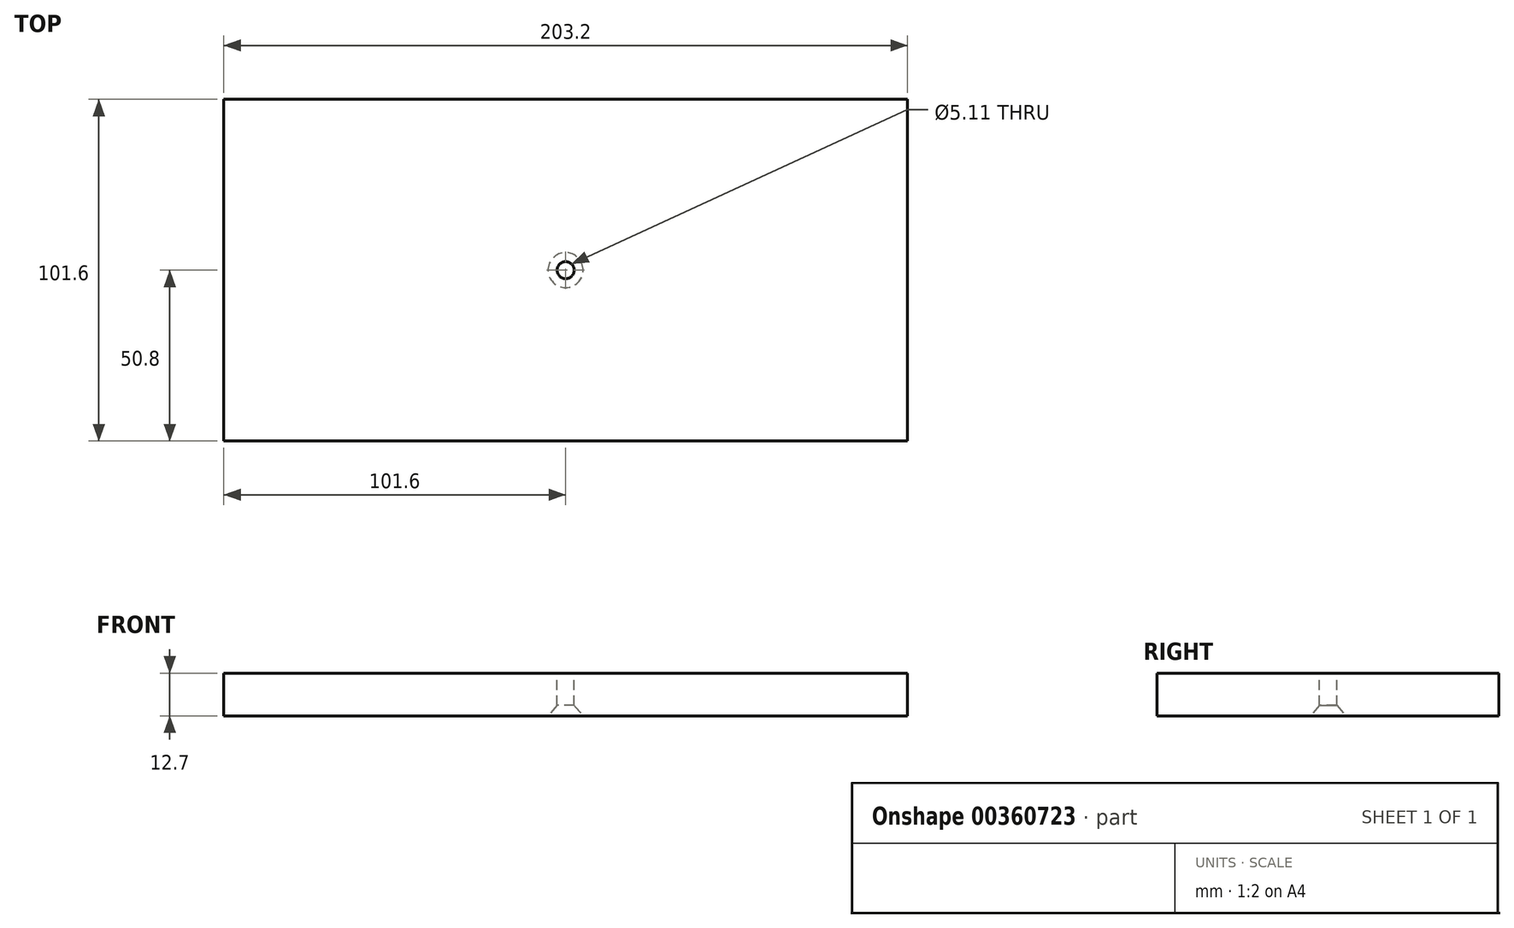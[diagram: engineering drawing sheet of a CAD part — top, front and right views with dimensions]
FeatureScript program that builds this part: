
annotation { "Feature Type Name" : "Feature", "Feature Type Description" : "" }
export const myFeature = defineFeature(function(context is Context, id is Id, definition is map)
    precondition{}
    {
        {
            var Q0;
            Q0=qCreatedBy(makeId("Top.planeOp"),FACE);
            var sketch = newSketch(context, id + "F0", { "sketchPlane" : qUnion([Q0])});
            skLineSegment(sketch, "E0.bottom", {"start": v(-101.6, 50.8) * mm, "end": v(101.6, 50.8) * mm});
            skLineSegment(sketch, "E0.top", {"start": v(-101.6, -50.8) * mm, "end": v(101.6, -50.8) * mm});
            skLineSegment(sketch, "E0.left", {"start": v(-101.6, 50.8) * mm, "end": v(-101.6, -50.8) * mm});
            skLineSegment(sketch, "E0.right", {"start": v(101.6, 50.8) * mm, "end": v(101.6, -50.8) * mm});
            skPoint(sketch, "E1", {"position": v(0, 50.8) * mm});
            skPoint(sketch, "E2", {"position": v(-101.6, 0) * mm});
            skSolve(sketch);
        }
        {
            var Q0;
            Q0=makeQuery(id+"F0.imprint","IMPRINT",FACE,{"disambiguationData":[TD([[makeQuery(id+"F0.imprint","IMPRINT",EDGE,{"derivedFrom":sQuery(id+"F0.wireOp",EDGE,"E0.bottom")}),-1.0]])]});
            extrude(context, id + "F1", {"entities" : qUnion([Q0]), "depth" : 12.7 * mm});
        }
        {
            var Q0;
            Q0=makeQuery(id+"F1.opExtrude","CAP_FACE",FACE,{"disambiguationData":[OSD([sQuery(id+"F0.wireOp",EDGE,"E0.bottom"),sQuery(id+"F0.wireOp",EDGE,"E0.top"),sQuery(id+"F0.wireOp",EDGE,"E0.left"),sQuery(id+"F0.wireOp",EDGE,"E0.right")])],"isStart":true});
            var sketch = newSketch(context, id + "F2", { "sketchPlane" : qUnion([Q0])});
            skPoint(sketch, "E3", {"position": v(0, 0) * mm});
            skSolve(sketch);
        }
        {
            var Q0;
            Q0=sQuery(id+"F2.wireOp",VERTEX,"E3");
            var Q1;
            Q1=makeQuery(id+"F1.opExtrude","SWEPT_BODY",BODY,{"disambiguationData":[OSD([sQuery(id+"F0.wireOp",EDGE,"E0.bottom"),sQuery(id+"F0.wireOp",EDGE,"E0.top"),sQuery(id+"F0.wireOp",EDGE,"E0.left"),sQuery(id+"F0.wireOp",EDGE,"E0.right")])]});
            hole(context, id + "F3", {"style" : HoleStyle.C_SINK, "endStyle" : HoleEndStyle.THROUGH, "standardTappedOrClearance" : lookupTablePath({ "standard" : "ANSI", "fit" : "Normal (ASME)", "size" : "#10", "type" : "Clearance" }), "standardBlindInLast" : lookupTablePath({ "fit" : "Free", "standard" : "ANSI", "size" : "#10", "type" : "Clearance" }), "holeDiameter" : 5.1 * mm, "cSinkDiameter" : 10.44 * mm, "cSinkAngle" : 82 * degree, "isTappedThrough" : true, "tappedDepth" : 12.7 * mm, "tapClearance" : 3, "locations" : qUnion([Q0]), "scope" : qUnion([Q1])});
        }
    });
